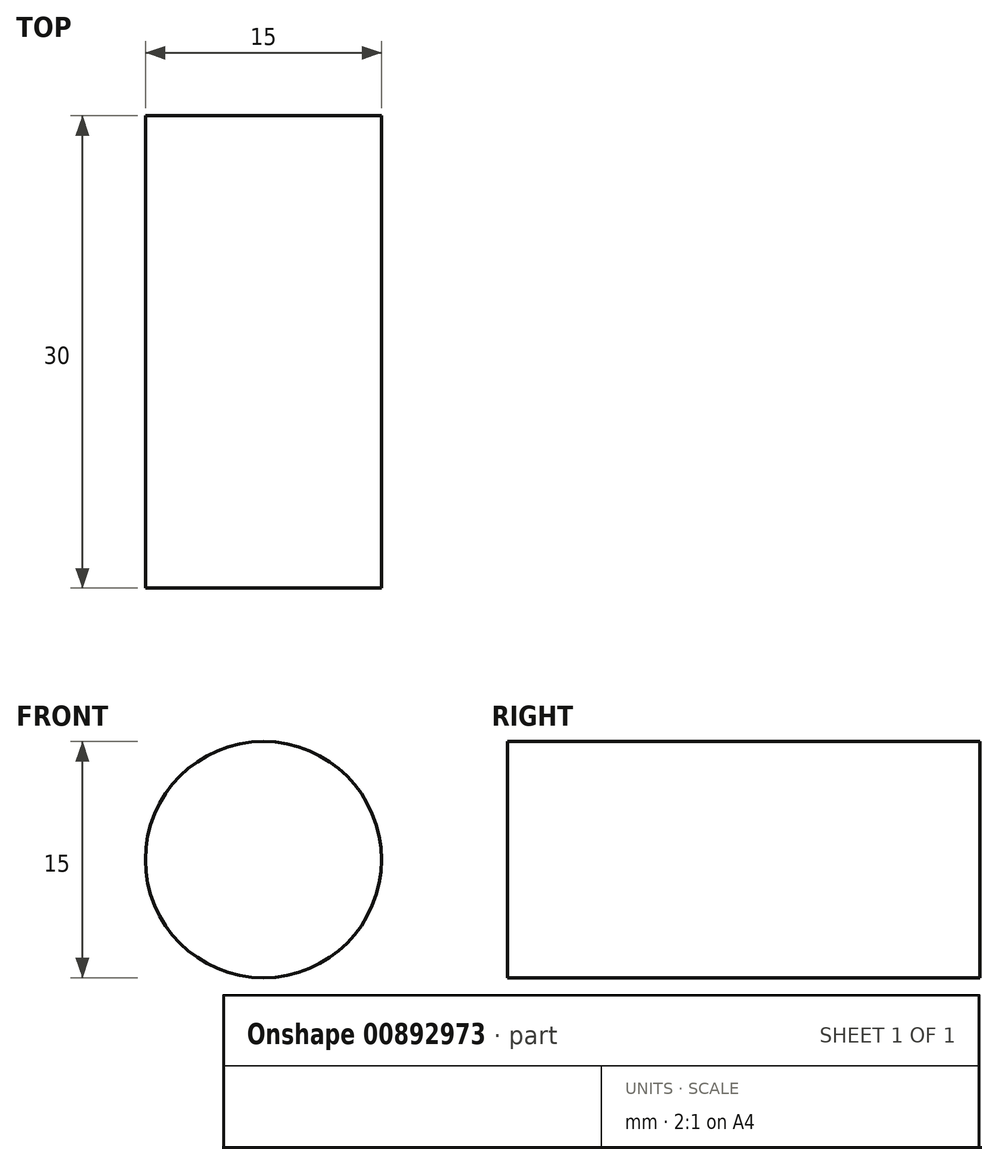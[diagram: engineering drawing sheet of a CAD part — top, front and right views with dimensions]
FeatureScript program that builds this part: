
annotation { "Feature Type Name" : "Feature", "Feature Type Description" : "" }
export const myFeature = defineFeature(function(context is Context, id is Id, definition is map)
    precondition{}
    {
        {
            var Q0;
            Q0=qCreatedBy(makeId("Front.planeOp"),FACE);
            var sketch = newSketch(context, id + "F0", { "sketchPlane" : qUnion([Q0])});
            skCircle(sketch, "E0", {"center": v(0, 0) * mm, "radius": 7.5 * mm});
            skSolve(sketch);
        }
        {
            var Q0;
            Q0 = qSketchRegion(id + "F0", true);
            extrude(context, id + "F1", {"entities" : qUnion([Q0]), "depth" : 30 * mm, "offsetDistance" : 25 * mm});
        }
    });
